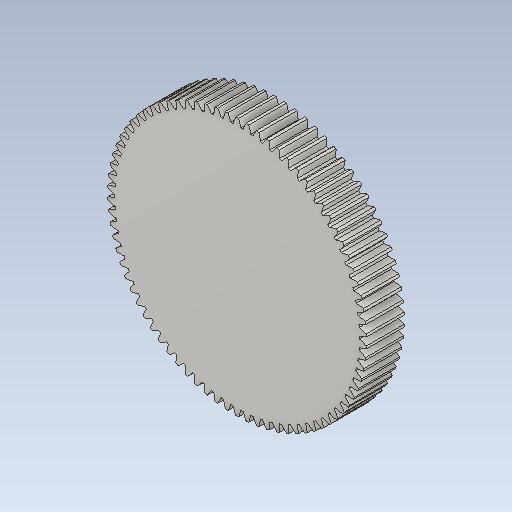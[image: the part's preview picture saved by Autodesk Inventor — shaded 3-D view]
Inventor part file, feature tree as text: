
AUTODESK INVENTOR PART (.ipt)
format: ipt  version: 2020.3 (Build 243373000, 373)  size: 474,112 bytes
history: native  units: mm (DEFAULTED — no unit token found)
features: plane x3, other x3, sketch x2, extrude x1
ambient origin geometry x8: Origin, YZ Plane, XZ Plane, XY Plane, X Axis, Y Axis, Z Axis, Center Point
bodies: Solid1 (feature_tree)
feature tree (9):
  extrude  "Extrusion1"  Depth=48.0mm TaperAngle=0.0deg
  plane  "Work Plane2"
  plane  "Work Plane8"
  plane  "Work Plane9"
  other  "Spur Gear"
  sketch  "Sketch1"  dims[d0=328.0mm d1=48.0mm d2=0.0mm]
  sketch  "Sketch2"  dims[d3=318.638298mm d4=10.0mm d5=0.0mm d16=192.0mm d17=0.0mm d34=0.402768mm d39=0.0mm d41=0.0mm d43=192.0mm d46=192.0mm d47=0.0mm d48=0.0mm]
  other  "Srf1"
  other  "Pitch Diameter"
